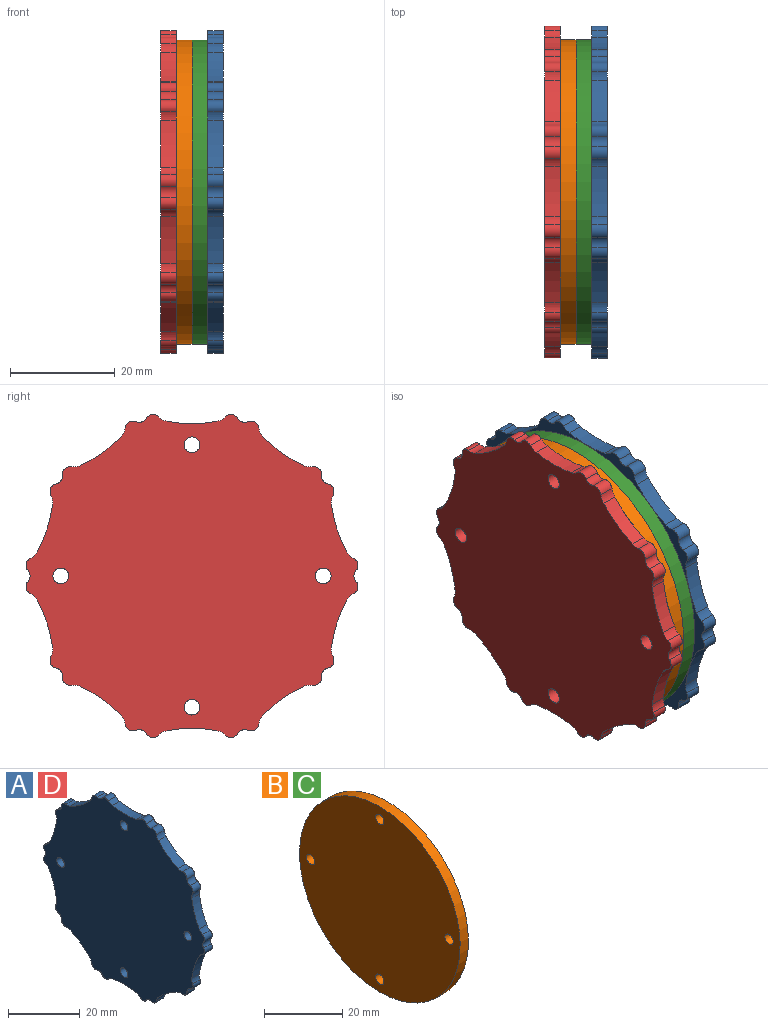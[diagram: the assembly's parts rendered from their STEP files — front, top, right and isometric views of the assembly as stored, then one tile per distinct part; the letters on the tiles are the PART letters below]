
ASSEMBLY  parts=4 mates=9
PART A: 66 faces, bbox 3x63.3x61.6 mm
  f0: plane 63.26x61.55mm, normal (1,0,0), area 2831.8mm2, adj f1,f2,f3,f4,f5,f7,f8,f9
  f1: cylinder r=1.5mm len=3mm, axis (-1,0,0), area 6.6mm2, adj f0,f2,f6,f14
  f2: cylinder r=1.5mm len=3mm, axis (-1,0,0), area 8.3mm2, adj f0,f1,f3,f6
  f3: cylinder r=3mm len=3mm, axis (-1,0,0), area 5.4mm2, adj f0,f2,f4,f6
  f4: cylinder r=25mm len=9.53mm, axis (-1,0,0), area 28.8mm2, adj f0,f3,f5,f6
  f5: cylinder r=3mm len=3mm, axis (-1,0,0), area 5.4mm2, adj f0,f4,f6,f7
  f6: plane 63.26x61.55mm, normal (-1,0,0), area 2831.8mm2, adj f1,f2,f3,f4,f5,f7,f8,f9
  f7: cylinder r=1.5mm len=3mm, axis (-1,0,0), area 8.3mm2, adj f0,f5,f6,f8
  f8: cylinder r=1.5mm len=3mm, axis (-1,0,0), area 6.6mm2, adj f0,f6,f7,f57
  f9: cylinder r=1.5mm len=3mm, axis (-1,0,0), area 6.6mm2, adj f0,f6,f10,f20
  f10: cylinder r=1.5mm len=3mm, axis (-1,0,0), area 8.3mm2, adj f0,f6,f9,f11
  f11: cylinder r=3mm len=3mm, axis (-1,0,0), area 5.4mm2, adj f0,f6,f10,f12
  f12: cylinder r=25mm len=7.71mm, axis (-1,0,0), area 28.8mm2, adj f0,f6,f11,f13
  f13: cylinder r=3mm len=3mm, axis (-1,0,0), area 5.4mm2, adj f0,f6,f12,f14
  f14: cylinder r=1.5mm len=3mm, axis (-1,0,0), area 8.3mm2, adj f0,f1,f6,f13
  f15: cylinder r=1.5mm len=3mm, axis (-1,0,0), area 6.6mm2, adj f0,f6,f16,f26
  f16: cylinder r=1.5mm len=3mm, axis (-1,0,0), area 8.3mm2, adj f0,f6,f15,f17
  f17: cylinder r=3mm len=3mm, axis (-1,0,0), area 5.4mm2, adj f0,f6,f16,f18
  f18: cylinder r=25mm len=9.06mm, axis (-1,0,0), area 28.8mm2, adj f0,f6,f17,f19
  f19: cylinder r=3mm len=3mm, axis (-1,0,0), area 5.4mm2, adj f0,f6,f18,f20
  f20: cylinder r=1.5mm len=3mm, axis (-1,0,0), area 8.3mm2, adj f0,f6,f9,f19
  f21: cylinder r=1.5mm len=3mm, axis (-1,0,0), area 6.6mm2, adj f0,f6,f22,f32
  f22: cylinder r=1.5mm len=3mm, axis (-1,0,0), area 8.3mm2, adj f0,f6,f21,f23
  f23: cylinder r=3mm len=3mm, axis (-1,0,0), area 5.4mm2, adj f0,f6,f22,f24
  f24: cylinder r=25mm len=9.06mm, axis (-1,0,0), area 28.8mm2, adj f0,f6,f23,f25
  f25: cylinder r=3mm len=3mm, axis (-1,0,0), area 5.4mm2, adj f0,f6,f24,f26
  f26: cylinder r=1.5mm len=3mm, axis (-1,0,0), area 8.3mm2, adj f0,f6,f15,f25
  f27: cylinder r=1.5mm len=3mm, axis (-1,0,0), area 6.6mm2, adj f0,f6,f28,f38
  f28: cylinder r=1.5mm len=3mm, axis (-1,0,0), area 8.3mm2, adj f0,f6,f27,f29
  f29: cylinder r=3mm len=3mm, axis (-1,0,0), area 5.4mm2, adj f0,f6,f28,f30
  f30: cylinder r=25mm len=7.71mm, axis (-1,0,0), area 28.8mm2, adj f0,f6,f29,f31
  f31: cylinder r=3mm len=3mm, axis (-1,0,0), area 5.4mm2, adj f0,f6,f30,f32
  f32: cylinder r=1.5mm len=3mm, axis (-1,0,0), area 8.3mm2, adj f0,f6,f21,f31
  f33: cylinder r=1.5mm len=3mm, axis (-1,0,0), area 6.6mm2, adj f0,f6,f34,f44
  f34: cylinder r=1.5mm len=3mm, axis (-1,0,0), area 8.3mm2, adj f0,f6,f33,f35
  f35: cylinder r=3mm len=3mm, axis (-1,0,0), area 5.4mm2, adj f0,f6,f34,f36
  f36: cylinder r=25mm len=9.53mm, axis (-1,0,0), area 28.8mm2, adj f0,f6,f35,f37
  f37: cylinder r=3mm len=3mm, axis (-1,0,0), area 5.4mm2, adj f0,f6,f36,f38
  f38: cylinder r=1.5mm len=3mm, axis (-1,0,0), area 8.3mm2, adj f0,f6,f27,f37
  f39: cylinder r=1.5mm len=3mm, axis (-1,0,0), area 6.6mm2, adj f0,f6,f40,f50
  f40: cylinder r=1.5mm len=3mm, axis (-1,0,0), area 8.3mm2, adj f0,f6,f39,f41
  f41: cylinder r=3mm len=3mm, axis (-1,0,0), area 5.4mm2, adj f0,f6,f40,f42
  f42: cylinder r=25mm len=7.71mm, axis (-1,0,0), area 28.8mm2, adj f0,f6,f41,f43
  f43: cylinder r=3mm len=3mm, axis (-1,0,0), area 5.4mm2, adj f0,f6,f42,f44
  f44: cylinder r=1.5mm len=3mm, axis (-1,0,0), area 8.3mm2, adj f0,f6,f33,f43
  f45: cylinder r=1.5mm len=3mm, axis (-1,0,0), area 6.6mm2, adj f0,f6,f46,f56
  f46: cylinder r=1.5mm len=3mm, axis (-1,0,0), area 8.3mm2, adj f0,f6,f45,f47
  f47: cylinder r=3mm len=3mm, axis (-1,0,0), area 5.4mm2, adj f0,f6,f46,f48
  f48: cylinder r=25mm len=9.06mm, axis (-1,0,0), area 28.8mm2, adj f0,f6,f47,f49
  f49: cylinder r=3mm len=3mm, axis (-1,0,0), area 5.4mm2, adj f0,f6,f48,f50
  f50: cylinder r=1.5mm len=3mm, axis (-1,0,0), area 8.3mm2, adj f0,f6,f39,f49
  f51: cylinder r=1.5mm len=3mm, axis (-1,0,0), area 6.6mm2, adj f0,f6,f52,f61
  f52: cylinder r=1.5mm len=3mm, axis (-1,0,0), area 8.3mm2, adj f0,f6,f51,f53
  f53: cylinder r=3mm len=3mm, axis (-1,0,0), area 5.4mm2, adj f0,f6,f52,f54
  f54: cylinder r=25mm len=9.06mm, axis (-1,0,0), area 28.8mm2, adj f0,f6,f53,f55
  f55: cylinder r=3mm len=3mm, axis (-1,0,0), area 5.4mm2, adj f0,f6,f54,f56
  f56: cylinder r=1.5mm len=3mm, axis (-1,0,0), area 8.3mm2, adj f0,f6,f45,f55
  f57: cylinder r=1.5mm len=3mm, axis (-1,0,0), area 8.3mm2, adj f0,f6,f8,f58
  f58: cylinder r=3mm len=3mm, axis (-1,0,0), area 5.4mm2, adj f0,f6,f57,f59
  f59: cylinder r=25mm len=7.71mm, axis (-1,0,0), area 28.8mm2, adj f0,f6,f58,f60
  f60: cylinder r=3mm len=3mm, axis (-1,0,0), area 5.4mm2, adj f0,f6,f59,f61
  f61: cylinder r=1.5mm len=3mm, axis (-1,0,0), area 8.3mm2, adj f0,f6,f51,f60
  f62: cylinder r=1.5mm len=3mm, axis (-1,0,0), area 28.3mm2, adj f0,f6
  f63: cylinder r=1.5mm len=3mm, axis (-1,0,0), area 28.3mm2, adj f0,f6
  f64: cylinder r=1.5mm len=3mm, axis (-1,0,0), area 28.3mm2, adj f0,f6
  f65: cylinder r=1.5mm len=3mm, axis (-1,0,0), area 28.3mm2, adj f0,f6
PART B: 7 faces, bbox 3x58x58 mm
  f0: plane 58x58mm, normal (1,0,0), area 2613.8mm2, adj f1,f3,f4,f5,f6
  f1: cylinder r=29mm len=58mm, axis (-1,0,0), area 546.6mm2, adj f0,f2
  f2: plane 58x58mm, normal (-1,0,0), area 2613.8mm2, adj f1,f3,f4,f5,f6
  f3: cylinder r=1.5mm len=3mm, axis (-1,0,0), area 28.3mm2, adj f0,f2
  f4: cylinder r=1.5mm len=3mm, axis (-1,0,0), area 28.3mm2, adj f0,f2
  f5: cylinder r=1.5mm len=3mm, axis (-1,0,0), area 28.3mm2, adj f0,f2
  f6: cylinder r=1.5mm len=3mm, axis (-1,0,0), area 28.3mm2, adj f0,f2
PART C: same geometry as B
PART D: same geometry as A
PLACE A t=(-47.8,0,0)mm fixed
PLACE B t=(-53.8,0,0)mm
PLACE C t=(-50.8,0,0)mm
PLACE D t=(-56.8,0,0)mm
MATE planar B.f1 <-> C.f1  axis (1,0,0) through (-50.8,0,33.28)mm
MATE planar C.f1 <-> A.f6  axis (1,0,0) through (-47.8,0,33.28)mm
MATE cylindrical D.f63 <-> B.f4  axis (-1,0,0) through (-55.3,25,33.28)mm
MATE planar D.f0 <-> B.f1  axis (1,0,0) through (-53.8,0,33.28)mm
MATE cylindrical A.f65 <-> C.f6  axis (-1,0,0) through (-47.8,-25,33.28)mm
MATE cylindrical B.f4 <-> C.f4  axis (-1,0,0) through (-52.3,25,33.28)mm
MATE cylindrical A.f63 <-> B.f4  axis (-1,0,0) through (-46.3,25,33.28)mm
MATE cylindrical D.f65 <-> B.f6  axis (-1,0,0) through (-53.8,-25,33.28)mm
MATE cylindrical C.f6 <-> B.f6  axis (-1,0,0) through (-49.3,-25,33.28)mm
